# Revit family: Stoßstellenverbinder - GSV 34 G.rfa.ok
name_source: partatom
category: Generic Models
revit_build: Autodesk Revit 2017 (Build: 20190508_0315(x64)
units: mm (PartAtom-declared; Revit-internal decimal feet)

## family parameters
Always vertical = Yes
Can host rebar = No
Cut with Voids When Loaded = No
Part Type = Normal
Room Calculation Point = No
Round Connector Dimension = Use Diameter
Shared = No
Work Plane-Based = No

## types (5) — shared parameters
Manufacturer = OBO BETTERMANN
URL = http://www.obo-bettermann.com

## per-type parameters (varying)
| type | GTIN | Manufacturer Art.No. | Material |
| GSV 34 G | 4012196520510 | 6016596 | galvanisch verzinkt |
| GSV 34 FT | 4012196013159 | 6016634 | Hot-dip galvanised |
| GSV 34 A2 | 4012196013210 | 6016642 | Stainless steel, A2 |
| GSV 34 A4 | 4012196120079 | 6016648 | Stainless steel, A4 |
| GSV 34 FTK LGR | 4012196333318 | 6479375 | PES50 - Polyester / epoxy |

note: column(s) folded — value = type name in every type: Article Type

## geometry (parser evidence)
native form markers: Sweep x2
no freeform markers — native parametric forms only
